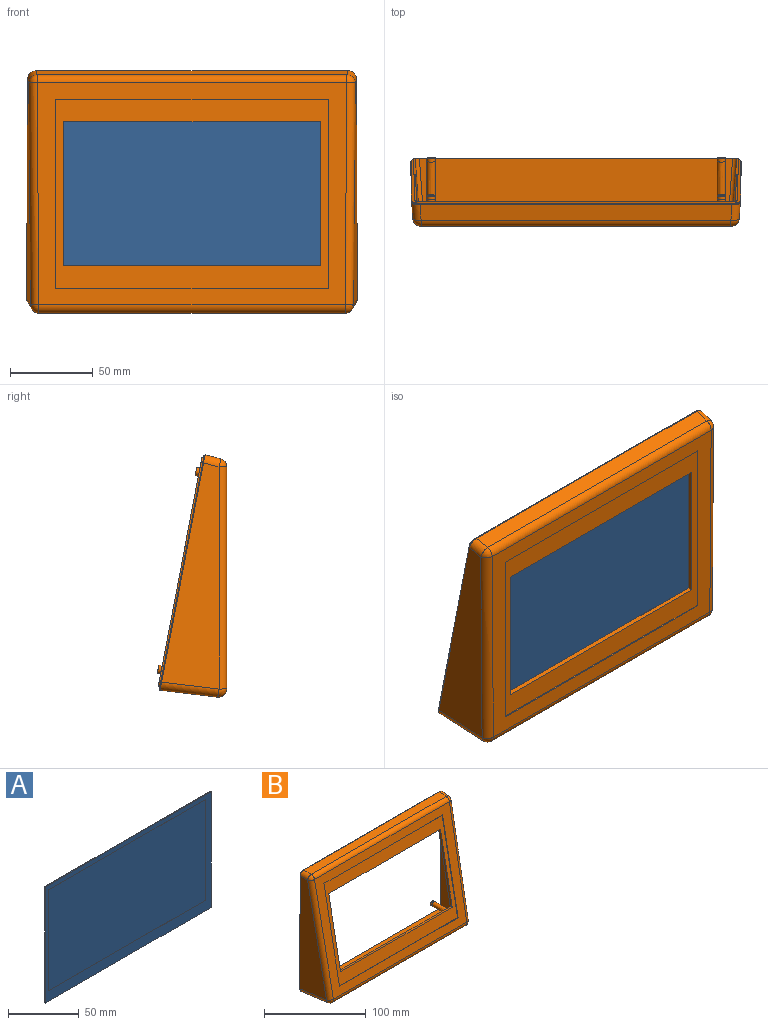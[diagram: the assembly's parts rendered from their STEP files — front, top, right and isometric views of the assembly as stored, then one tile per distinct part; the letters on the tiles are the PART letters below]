
ASSEMBLY  parts=2 mates=1
PART A: 11 faces, bbox 165x0.8x100 mm
  f0: plane 100x0.75mm, normal (-1,0,0), area 75mm2, adj f1,f3,f4,f9
  f1: plane 165x0.75mm, normal (0,0,-1), area 123.8mm2, adj f0,f2,f4,f9
  f2: plane 100x0.75mm, normal (1,0,0), area 75mm2, adj f1,f3,f4,f9
  f3: plane 165x0.75mm, normal (0,0,1), area 123.8mm2, adj f0,f2,f4,f9
  f4: plane 165x100mm, normal (0,1,0), area 16500mm2, adj f0,f1,f2,f3
  f5: plane 87x0.05mm, normal (1,0,0), area 4.4mm2, adj f6,f8,f9,f10
  f6: plane 156x0.05mm, normal (0,0,-1), area 7.8mm2, adj f5,f7,f9,f10
  f7: plane 87x0.05mm, normal (-1,0,0), area 4.4mm2, adj f6,f8,f9,f10
  f8: plane 156x0.05mm, normal (0,0,1), area 7.8mm2, adj f5,f7,f9,f10
  f9: plane 165x100mm, normal (0,-1,0), area 2928mm2, adj f0,f1,f2,f3,f5,f6,f7,f8
  f10: plane 156x87mm, normal (0,-1,0), area 13572mm2, adj f5,f6,f7,f8
PART B: 87 faces, bbox 200x43.3x145.1 mm
  f0: plane 190.08x134.68mm, normal (0,0.98,-0.19), area 5344.2mm2, adj f5,f6,f7,f8,f16,f17,f18,f19
  f1: plane 198.74x143.79mm, normal (0,1,0), area 872.8mm2, adj f24,f25,f26,f27,f28,f29,f30,f31
  f2: plane 196.28x141.33mm, normal (0,1,0), area 664.2mm2, adj f3,f4,f10,f11,f12,f13,f14,f15
  f3: plane 187.84x12.19mm, normal (0,0.07,-1), area 2284.5mm2, adj f2,f13,f15,f16
  f4: plane 189.15x37.98mm, normal (0,0.07,1), area 7099mm2, adj f2,f12,f14,f23
  f5: plane 170.3x0.69mm, normal (0,0.19,0.98), area 119.2mm2, adj f0,f6,f8,f9
  f6: plane 118.29x23.31mm, normal (-1,0,0), area 84.2mm2, adj f0,f5,f7,f9
  f7: plane 170.3x0.69mm, normal (0,-0.19,-0.98), area 119.2mm2, adj f0,f6,f8,f9
  f8: plane 118.29x23.31mm, normal (1,0,0), area 84.2mm2, adj f0,f5,f7,f9
  f9: plane 170.3x118.15mm, normal (0,0.98,-0.19), area 7002.1mm2, adj f5,f6,f7,f8,f83,f84,f85,f86
  f10: plane 134.2x37.6mm, normal (1,0.07,0), area 3341.4mm2, adj f2,f12,f13,f20
  f11: plane 134.2x37.6mm, normal (-1,0.07,0), area 3341.4mm2, adj f2,f14,f15,f19
  f12: cylinder r=2.5mm len=38.05mm, axis (-0.07,1,-0.07), area 149.1mm2, adj f2,f4,f10,f22
  f13: cylinder r=2.5mm len=12.64mm, axis (-0.07,1,0.07), area 48.6mm2, adj f2,f3,f10,f18
  f14: cylinder r=2.5mm len=38.05mm, axis (-0.07,-1,0.07), area 149.1mm2, adj f2,f4,f11,f21
  f15: cylinder r=2.5mm len=12.64mm, axis (-0.07,-1,-0.07), area 48.6mm2, adj f2,f3,f11,f17
  f16: cylinder r=0.5mm len=186.14mm, axis (1,0,0), area 122.1mm2, adj f0,f3,f17,f18
  f17: bspline ~2.51x2.47mm, area 2.5mm2, adj f0,f15,f16,f19
  f18: bspline ~2.51x2.47mm, area 2.5mm2, adj f0,f13,f16,f20
  f19: cylinder r=0.5mm len=130.78mm, axis (-0.01,-0.19,-0.98), area 99.9mm2, adj f0,f11,f17,f21
  f20: cylinder r=0.5mm len=130.78mm, axis (-0.01,0.19,0.98), area 99.9mm2, adj f0,f10,f18,f22
  f21: bspline ~2.98x2.64mm, area 2.9mm2, adj f0,f14,f19,f23
  f22: bspline ~2.57x2.52mm, area 2.9mm2, adj f0,f12,f20,f23
  f23: cylinder r=0.5mm len=183.82mm, axis (1,0,0), area 155.3mm2, adj f0,f4,f21,f22
  f24: extruded ~3.49x3.48mm, area 5.5mm2, adj f1,f2,f25,f31
  f25: plane 187.84x1mm, normal (0,0,1), area 187.8mm2, adj f1,f2,f24,f26
  f26: extruded ~3.49x3.48mm, area 5.5mm2, adj f1,f2,f25,f27
  f27: plane 134.2x1mm, normal (-1,0,0), area 134.2mm2, adj f1,f2,f26,f28
  f28: extruded ~3.51x3.49mm, area 5.5mm2, adj f1,f2,f27,f29
  f29: plane 189.15x1mm, normal (0,0,-1), area 189.1mm2, adj f1,f2,f28,f30
  f30: extruded ~3.51x3.49mm, area 5.5mm2, adj f1,f2,f29,f31
  f31: plane 134.2x1mm, normal (1,0,0), area 134.2mm2, adj f1,f2,f24,f30
  f32: plane 200.03x145.08mm, normal (0,1,0), area 342.8mm2, adj f33,f34,f35,f36,f37,f38,f39,f40
  f33: extruded ~4.79x4.77mm, area 3.8mm2, adj f1,f32,f34,f40
  f34: plane 187.84x0.5mm, normal (0,0,1), area 93.9mm2, adj f1,f32,f33,f35
  f35: extruded ~4.79x4.77mm, area 3.8mm2, adj f1,f32,f34,f36
  f36: plane 134.2x0.65mm, normal (-1,0,0), area 67.1mm2, adj f1,f32,f35,f37
  f37: extruded ~4.82x4.79mm, area 3.8mm2, adj f1,f32,f36,f38
  f38: plane 189.15x0.5mm, normal (0,0,-1), area 94.6mm2, adj f1,f32,f37,f39
  f39: extruded ~4.82x4.79mm, area 3.8mm2, adj f1,f32,f38,f40
  f40: plane 134.2x0.65mm, normal (1,0,0), area 67.1mm2, adj f1,f32,f33,f39
  f41: plane 164.5x112.46mm, normal (0,-0.98,0.19), area 5350.2mm2, adj f42,f43,f44,f45,f83,f84,f85,f86
  f42: plane 112.59x22.22mm, normal (1,0,0), area 80.1mm2, adj f41,f43,f45,f46
  f43: plane 164.5x0.69mm, normal (0,0.19,0.98), area 115.1mm2, adj f41,f42,f44,f46
  f44: plane 112.59x22.22mm, normal (-1,0,0), area 80.1mm2, adj f41,f43,f45,f46
  f45: plane 164.5x0.69mm, normal (0,-0.19,-0.98), area 115.1mm2, adj f41,f42,f44,f46
  f46: plane 187.11x131.7mm, normal (0,-0.98,0.19), area 6104.9mm2, adj f42,f43,f44,f45,f49,f52,f53,f54
  f47: sphere r=5mm, area 31.3mm2, adj f49,f54,f62
  f48: sphere r=5mm, area 40.3mm2, adj f49,f53,f61
  f49: cylinder r=5mm len=132.62mm, axis (0.01,-0.19,-0.98), area 1006.7mm2, adj f46,f47,f48,f60
  f50: sphere r=5mm, area 31.3mm2, adj f52,f54,f59
  f51: sphere r=5mm, area 40.3mm2, adj f52,f53,f58
  f52: cylinder r=5mm len=132.62mm, axis (0.01,0.19,0.98), area 1006.7mm2, adj f46,f50,f51,f56
  f53: cylinder r=5mm len=184.88mm, axis (-1,0,0), area 1562.3mm2, adj f46,f48,f51,f57
  f54: cylinder r=5mm len=187.11mm, axis (-1,0,0), area 1227.2mm2, adj f46,f47,f50,f55
  f55: plane 188.45x9.66mm, normal (0,-0.07,1), area 1818.7mm2, adj f32,f54,f59,f62
  f56: plane 134.81x34.88mm, normal (1,-0.07,0), area 2985.9mm2, adj f32,f52,f58,f59
  f57: plane 189.77x34.88mm, normal (0,-0.07,-1), area 6549.4mm2, adj f32,f53,f58,f61
  f58: cylinder r=5mm len=35.02mm, axis (0.07,1,-0.07), area 275.3mm2, adj f32,f51,f56,f57
  f59: cylinder r=5mm len=9.8mm, axis (0.07,1,0.07), area 75.8mm2, adj f32,f50,f55,f56
  f60: plane 134.81x34.88mm, normal (-1,-0.07,0), area 2985.9mm2, adj f32,f49,f61,f62
  f61: cylinder r=5mm len=35.02mm, axis (0.07,-1,0.07), area 275.3mm2, adj f32,f48,f57,f60
  f62: cylinder r=5mm len=9.8mm, axis (0.07,-1,-0.07), area 75.8mm2, adj f32,f47,f55,f60
  f63: bspline ~37.7x5mm, area 582.9mm2, adj f0,f64
  f64: cylinder r=2.5mm len=5mm, axis (0,-1,0), area 31.4mm2, adj f63,f65
  f65: plane 5x5mm, normal (0,1,0), area 12.6mm2, adj f64,f66
  f66: cylinder r=1.5mm len=37mm, axis (0,-1,0), area 348.7mm2, adj f65,f67
  f67: cone r=0mm half-angle=59deg, axis (0,1,0), area 8.2mm2, adj f66
  f68: bspline ~37.72x5mm, area 583.2mm2, adj f0,f69
  f69: cylinder r=2.5mm len=5mm, axis (0,-1,0), area 31.4mm2, adj f68,f70
  f70: plane 5x5mm, normal (0,1,0), area 12.6mm2, adj f69,f71
  f71: cylinder r=1.5mm len=37mm, axis (0,-1,0), area 348.7mm2, adj f70,f72
  f72: cone r=0mm half-angle=59deg, axis (0,1,0), area 8.2mm2, adj f71
  f73: bspline ~14.44x5mm, area 218.5mm2, adj f0,f74
  f74: cylinder r=2.5mm len=5mm, axis (0,-1,0), area 31.4mm2, adj f73,f75
  f75: plane 5x5mm, normal (0,1,0), area 12.6mm2, adj f74,f79
  f76: bspline ~14.42x5.02mm, area 218.2mm2, adj f0,f77
  f77: cylinder r=2.5mm len=5mm, axis (0,-1,0), area 31.4mm2, adj f76,f78
  f78: plane 5x5mm, normal (0,1,0), area 12.6mm2, adj f77,f81
  f79: cylinder r=1.5mm len=15mm, axis (0,-1,0), area 141.4mm2, adj f75,f80
  f80: cone r=0mm half-angle=59deg, axis (0,1,0), area 8.2mm2, adj f79
  f81: cylinder r=1.5mm len=15mm, axis (0,-1,0), area 141.4mm2, adj f78,f82
  f82: cone r=0mm half-angle=59deg, axis (0,1,0), area 8.2mm2, adj f81
  f83: plane 155x2.85mm, normal (0,-0.19,-0.98), area 449.5mm2, adj f9,f41,f84,f86
  f84: plane 85.99x19.21mm, normal (1,0,0), area 252.3mm2, adj f9,f41,f83,f85
  f85: plane 155x2.85mm, normal (0,0.19,0.98), area 449.5mm2, adj f9,f41,f84,f86
  f86: plane 85.99x19.21mm, normal (-1,0,0), area 252.3mm2, adj f9,f41,f83,f85
PLACE A t=(-75.8,2.75,-29.83)mm
PLACE B rot(axis=(1,0,0),10.8deg) t=(11.58,28.76,15)mm
MATE fastened A.f10 <-> B.f9  axis (0,-1,0) through (83.2,2.05,22.67)mm
